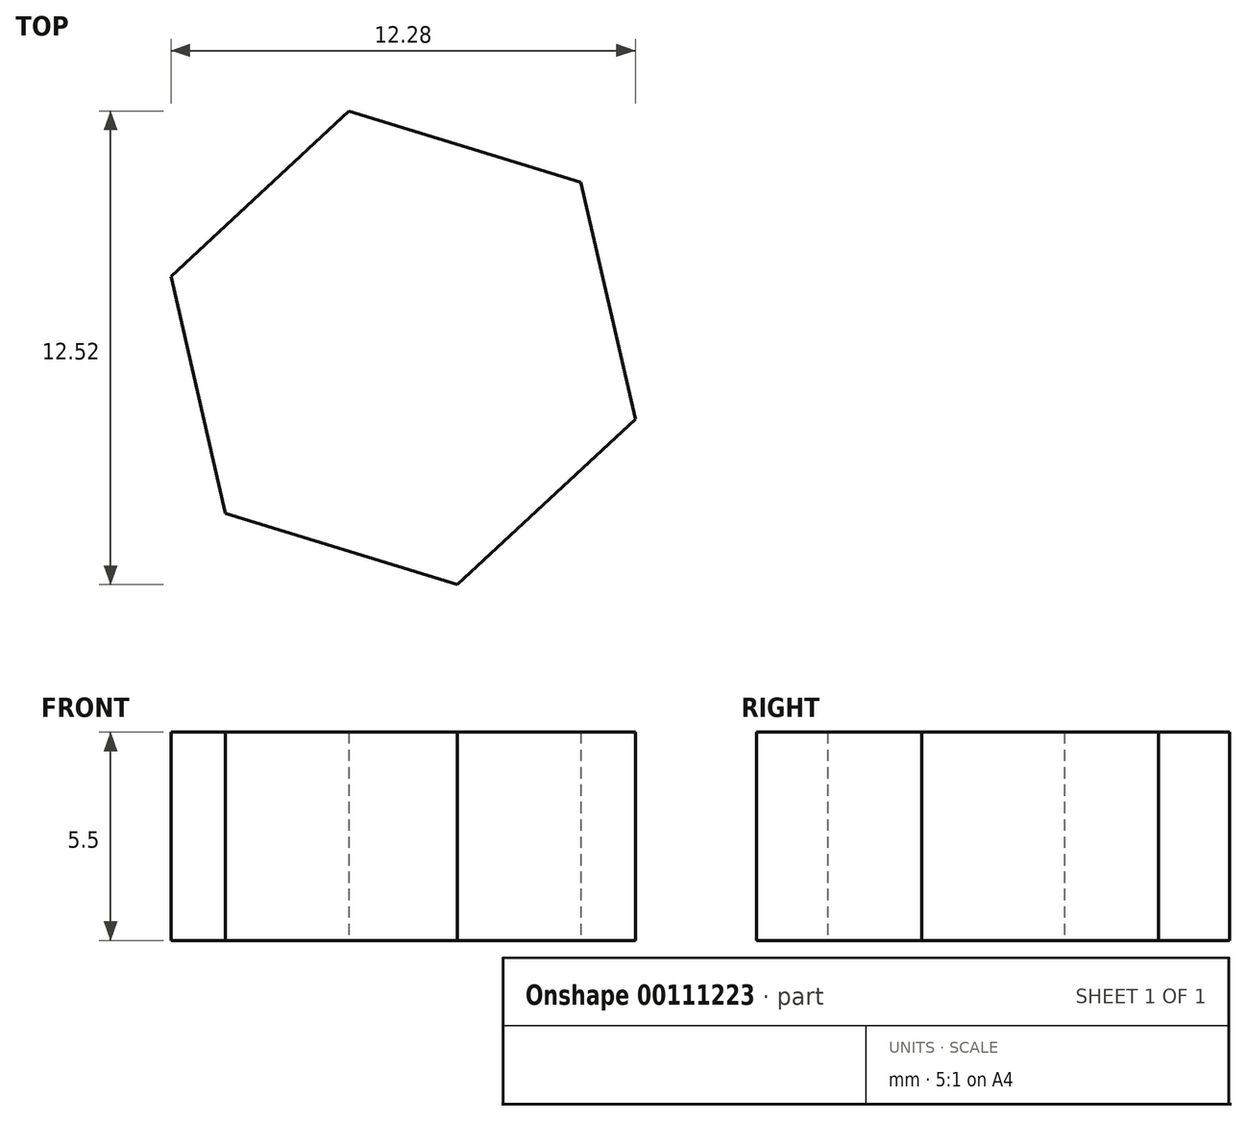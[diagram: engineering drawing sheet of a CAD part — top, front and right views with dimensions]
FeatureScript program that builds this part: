
annotation { "Feature Type Name" : "Feature", "Feature Type Description" : "" }
export const myFeature = defineFeature(function(context is Context, id is Id, definition is map)
    precondition{}
    {
        {
            var Q0;
            Q0=qCreatedBy(makeId("Top.planeOp"),FACE);
            var sketch = newSketch(context, id + "F0", { "sketchPlane" : qUnion([Q0])});
            skCircle(sketch, "E0.cCircle", {"center": v(0, 0) * mm, "radius": 5.56 * mm, "construction": true});
            skLineSegment(sketch, "E0.0", {"start": v(6.14, -1.88) * mm, "end": v(1.44, -6.26) * mm});
            skLineSegment(sketch, "E0.1", {"start": v(1.44, -6.26) * mm, "end": v(-4.7, -4.37) * mm});
            skLineSegment(sketch, "E0.2", {"start": v(-4.7, -4.37) * mm, "end": v(-6.14, 1.88) * mm});
            skLineSegment(sketch, "E0.3", {"start": v(-6.14, 1.88) * mm, "end": v(-1.44, 6.26) * mm});
            skLineSegment(sketch, "E0.4", {"start": v(-1.44, 6.26) * mm, "end": v(4.7, 4.37) * mm});
            skLineSegment(sketch, "E0.5", {"start": v(4.7, 4.37) * mm, "end": v(6.14, -1.88) * mm});
            skPoint(sketch, "E0.0.midPoint", {"position": v(3.79, -4.07) * mm});
            skSolve(sketch);
        }
        {
            var Q0;
            Q0 = qSketchRegion(id + "FNXwQEQn09yuz1E_0", true);
            var Q1;
            Q1=makeQuery(id+"F0.imprint","IMPRINT",FACE,{"disambiguationData":[TD([[makeQuery(id+"F0.imprint","IMPRINT",EDGE,{"derivedFrom":sQuery(id+"F0.wireOp",EDGE,"E0.0")}),-1.0]])]});
            extrude(context, id + "F1", {"entities" : qUnion([Q0, Q1]), "depth" : 5.5 * mm});
        }
    });
